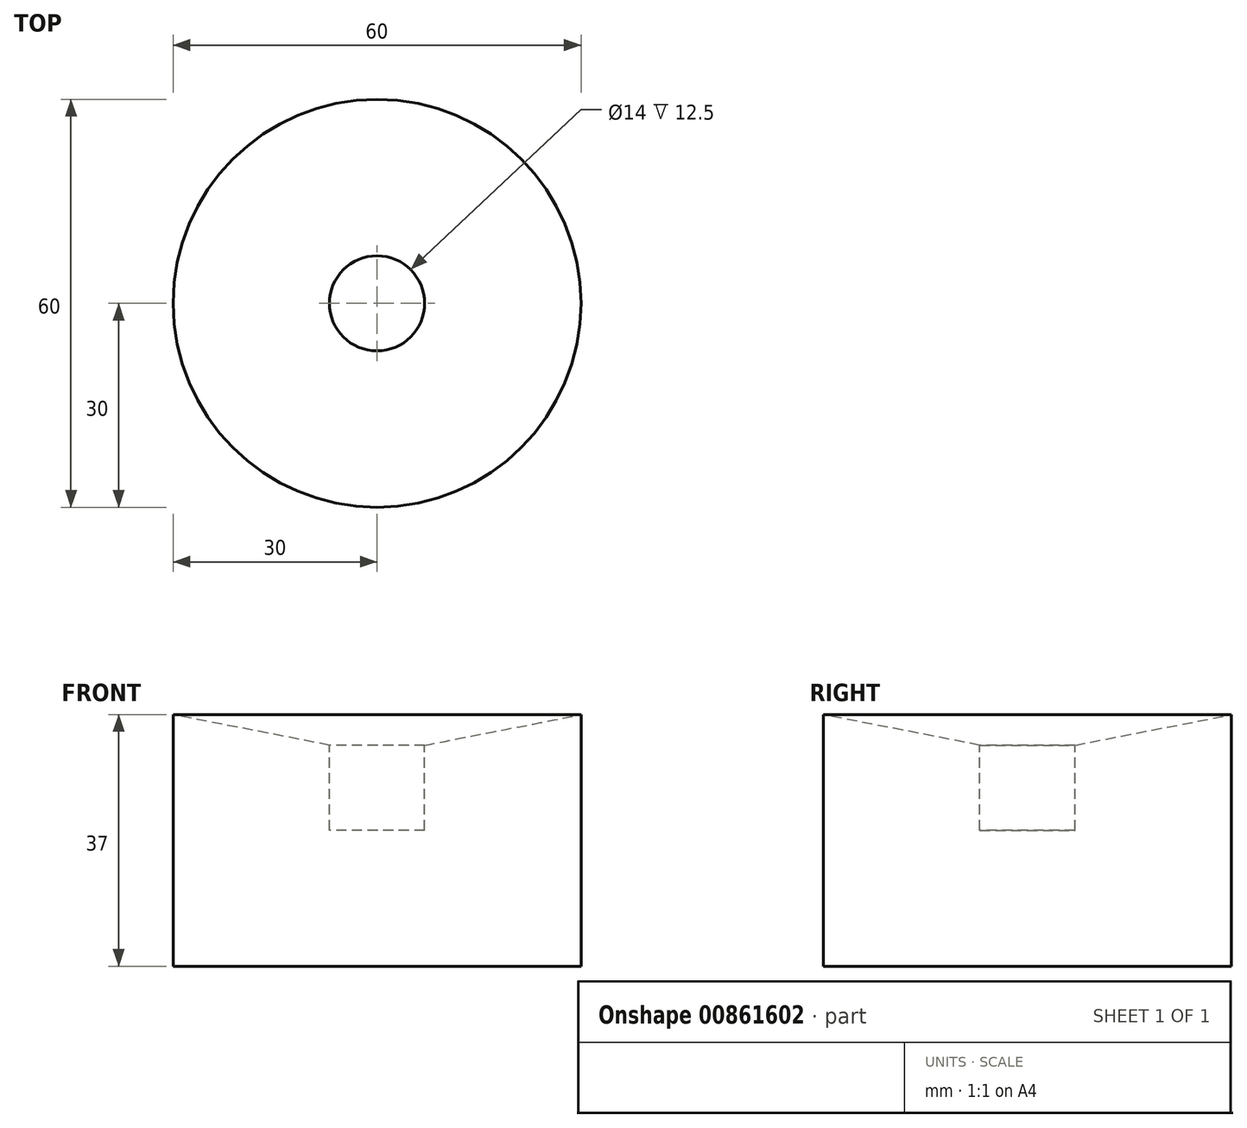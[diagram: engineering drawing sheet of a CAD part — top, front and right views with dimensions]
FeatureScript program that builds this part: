
annotation { "Feature Type Name" : "Feature", "Feature Type Description" : "" }
export const myFeature = defineFeature(function(context is Context, id is Id, definition is map)
    precondition{}
    {
        {
            var Q0;
            Q0=qCreatedBy(makeId("Front.planeOp"),FACE);
            var sketch = newSketch(context, id + "F0", { "sketchPlane" : qUnion([Q0])});
            skLineSegment(sketch, "E0", {"start": v(0, 0) * mm, "end": v(-30, 0) * mm});
            skLineSegment(sketch, "E1", {"start": v(-30, 0) * mm, "end": v(-30, 37) * mm});
            skLineSegment(sketch, "E2", {"start": v(-30, 37) * mm, "end": v(-7, 32.5) * mm});
            skLineSegment(sketch, "E3", {"start": v(-7, 32.5) * mm, "end": v(-7, 20) * mm});
            skLineSegment(sketch, "E4", {"start": v(-7, 20) * mm, "end": v(0, 20) * mm});
            skLineSegment(sketch, "E5", {"start": v(0, 20) * mm, "end": v(0, 0) * mm});
            skSolve(sketch);
        }
        {
            var Q0;
            Q0 = qSketchRegion(id + "F0", true);
            var Q1;
            Q1=sQuery(id+"F0.wireOp",EDGE,"E5");
            revolve(context, id + "F1", {"surfaceOperationType" : NewSurfaceOperationType.NEW, "entities" : qUnion([Q0]), "axis" : qUnion([Q1]), "revolveType" : RevolveType.FULL});
        }
    });
